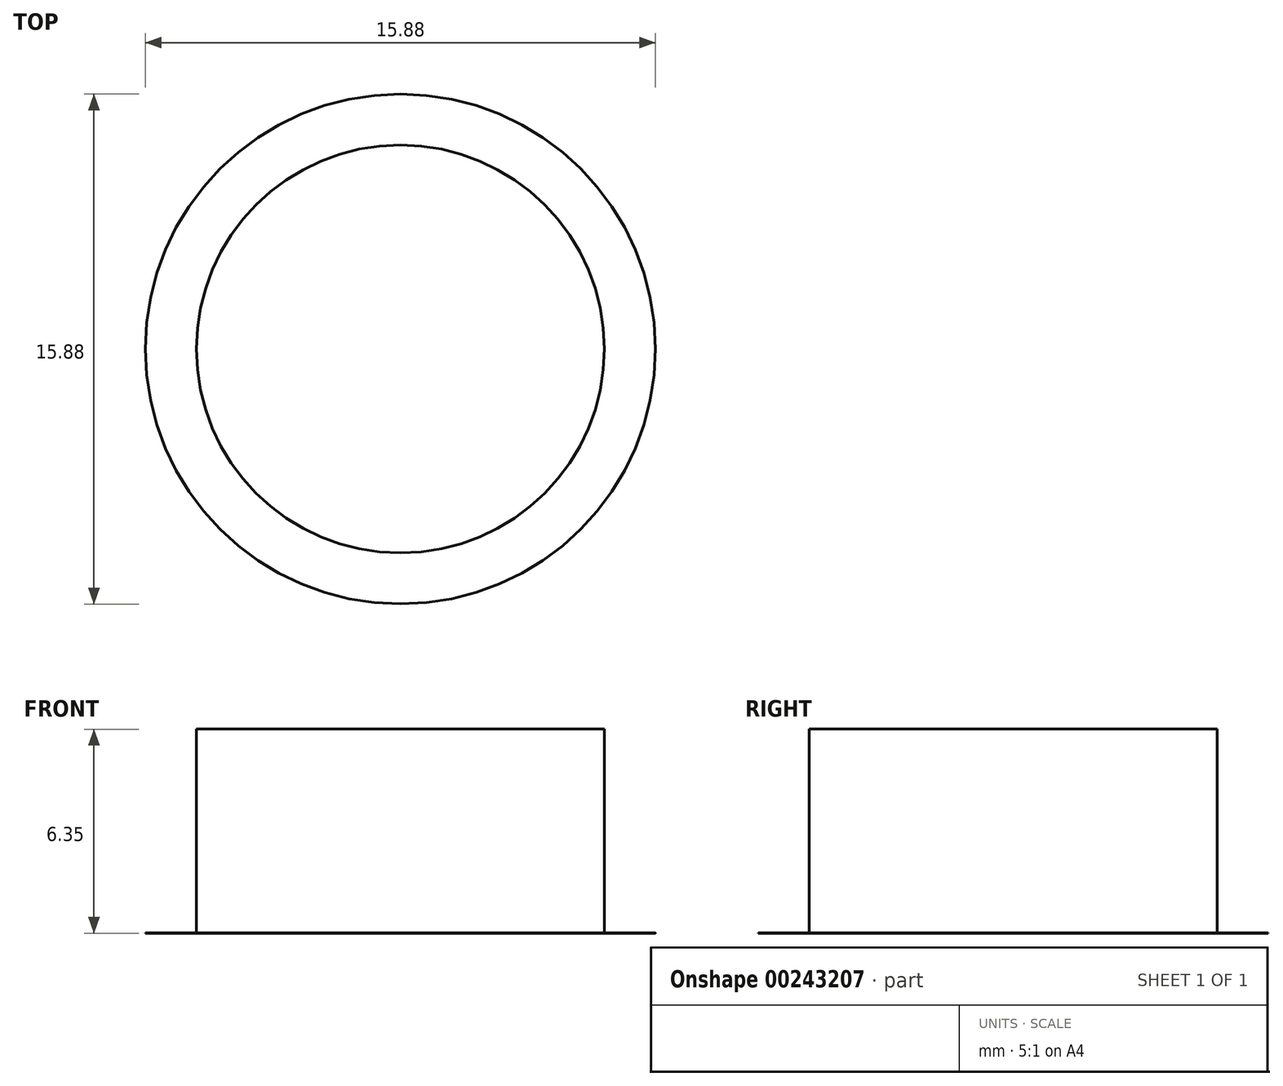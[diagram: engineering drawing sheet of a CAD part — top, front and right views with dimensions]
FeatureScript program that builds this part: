
annotation { "Feature Type Name" : "Feature", "Feature Type Description" : "" }
export const myFeature = defineFeature(function(context is Context, id is Id, definition is map)
    precondition{}
    {
        {
            var Q0;
            Q0=qCreatedBy(makeId("Top.planeOp"),FACE);
            var sketch = newSketch(context, id + "F0", { "sketchPlane" : qUnion([Q0])});
            skCircle(sketch, "E0", {"center": v(0, 0) * mm, "radius": 7.94 * mm});
            skSolve(sketch);
        }
        {
            var Q0;
            Q0 = qSketchRegion(id + "F0", true);
            extrude(context, id + "F1", {"entities" : qUnion([Q0]), "depth" : 1 / 406.4 * mm});
        }
        {
            var Q0;
            Q0=makeQuery(id+"F1.opExtrude","CAP_FACE",FACE,{"disambiguationData":[OSD([sQuery(id+"F0.wireOp",EDGE,"E0")])],"isStart":false});
            var sketch = newSketch(context, id + "F2", { "sketchPlane" : qUnion([Q0])});
            skCircle(sketch, "E1", {"center": v(0, 0) * mm, "radius": 6.35 * mm});
            skSolve(sketch);
        }
        {
            var Q0;
            Q0 = qSketchRegion(id + "F2", true);
            extrude(context, id + "F3", {"entities" : qUnion([Q0]), "operationType" : NewBodyOperationType.ADD, "depth" : 6.35 * mm});
        }
    });
